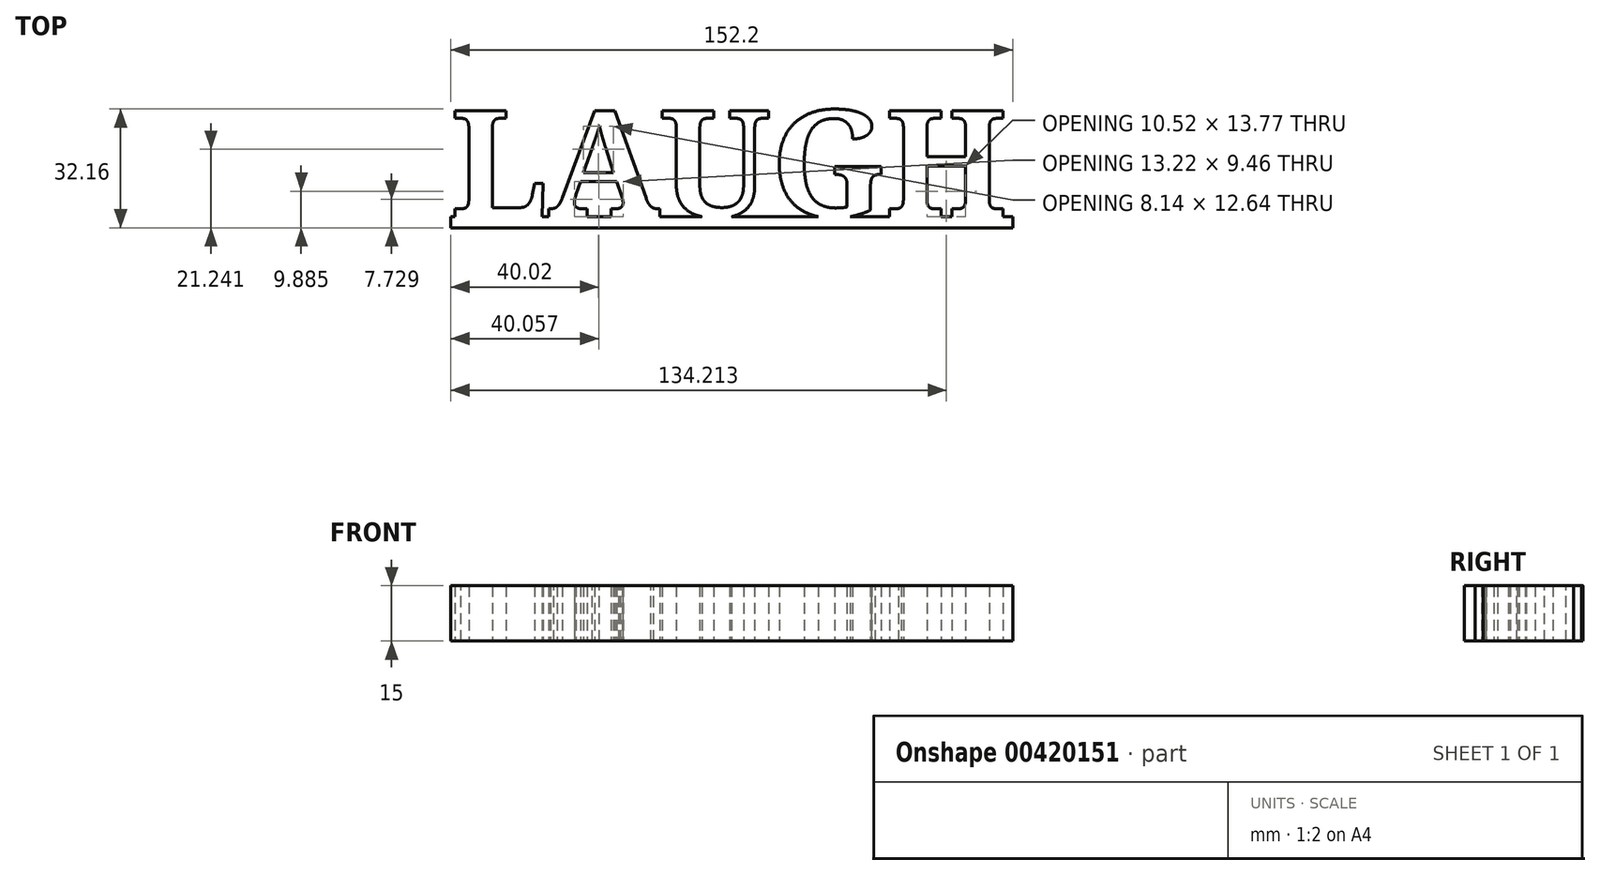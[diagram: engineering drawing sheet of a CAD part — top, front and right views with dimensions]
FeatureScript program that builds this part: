
annotation { "Feature Type Name" : "Feature", "Feature Type Description" : "" }
export const myFeature = defineFeature(function(context is Context, id is Id, definition is map)
    precondition{}
    {
        {
            var Q0;
            Q0=qCreatedBy(makeId("Top.planeOp"),FACE);
            var sketch = newSketch(context, id + "F0", { "sketchPlane" : qUnion([Q0])});
            skText(sketch, "E0", { "text": "LAUGH", "fontName": "NotoSerif-Bold.ttf"});
            skLineSegment(sketch, "E1", {"start": v(0, 0) * mm, "end": v(152.2, 0) * mm});
            skLineSegment(sketch, "E2", {"start": v(152.2, -3) * mm, "end": v(0, -3) * mm});
            skLineSegment(sketch, "E3", {"start": v(0, -3) * mm, "end": v(0, 0) * mm});
            skLineSegment(sketch, "E4", {"start": v(152.2, 0) * mm, "end": v(152.2, -3) * mm});
            const initialGuessF0  = {"E0": [0, 0, 1, 0, 0.029]};
            skSetInitialGuess(sketch, initialGuessF0);
            skSolve(sketch);
        }
        {
            var Q0;
            Q0=qSketchRegion(id+"F0",true);
            extrude(context, id + "F1", {"entities" : qUnion([Q0]), "depth" : 15 * mm});
        }
    });
